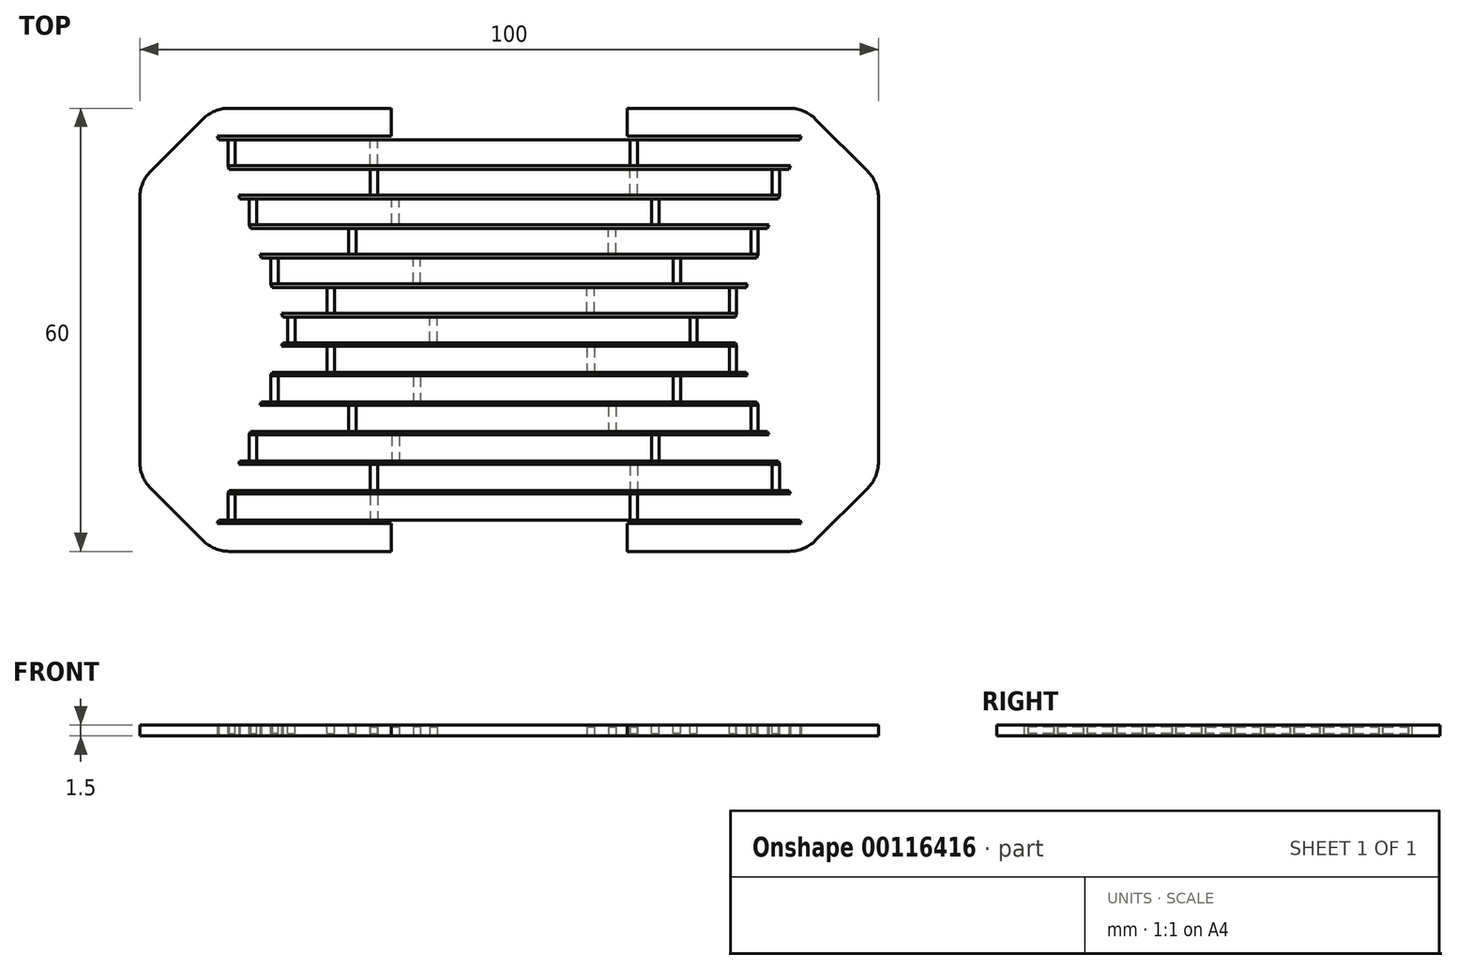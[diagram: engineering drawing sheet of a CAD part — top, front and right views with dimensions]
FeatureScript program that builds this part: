
annotation { "Feature Type Name" : "Feature", "Feature Type Description" : "" }
export const myFeature = defineFeature(function(context is Context, id is Id, definition is map)
    precondition{}
    {
        {
            var Q0;
            Q0=qCreatedBy(makeId("Top.planeOp"),FACE);
            var sketch = newSketch(context, id + "F0", { "sketchPlane" : qUnion([Q0])});
            skLineSegment(sketch, "E0.bottom", {"start": v(-50, 30) * mm, "end": v(-13.55, 30) * mm});
            skLineSegment(sketch, "E0.top", {"start": v(-50, -30) * mm, "end": v(-13.55, -30) * mm});
            skLineSegment(sketch, "E0.left", {"start": v(-50, 30) * mm, "end": v(-50, -30) * mm});
            skLineSegment(sketch, "E0.right", {"start": v(50, 30) * mm, "end": v(50, -30) * mm});
            skPoint(sketch, "E0.middle", {"position": v(0, 0) * mm});
            skLineSegment(sketch, "E1", {"start": v(-39.54, 26.25) * mm, "end": v(-39.36, 25.75) * mm});
            skLineSegment(sketch, "E2", {"start": v(-30.62, -1.75) * mm, "end": v(-30.8, -2.25) * mm});
            skLineSegment(sketch, "E3", {"start": v(-39.54, 26.25) * mm, "end": v(-13.55, 26.25) * mm});
            skLineSegment(sketch, "E4", {"start": v(-39.36, 25.75) * mm, "end": v(39.36, 25.75) * mm});
            skLineSegment(sketch, "E5", {"start": v(-38.08, 22.25) * mm, "end": v(38.08, 22.25) * mm});
            skLineSegment(sketch, "E6", {"start": v(-37.9, 21.75) * mm, "end": v(37.9, 21.75) * mm});
            skLineSegment(sketch, "E7.0.1.0", {"start": v(-36.63, 18.25) * mm, "end": v(36.63, 18.25) * mm});
            skLineSegment(sketch, "E7.0.1.1", {"start": v(-36.45, 17.75) * mm, "end": v(36.45, 17.75) * mm});
            skLineSegment(sketch, "E7.0.2.0", {"start": v(-35.17, 14.25) * mm, "end": v(35.17, 14.25) * mm});
            skLineSegment(sketch, "E7.0.2.1", {"start": v(-34.99, 13.75) * mm, "end": v(34.99, 13.75) * mm});
            skLineSegment(sketch, "E7.0.3.0", {"start": v(-33.72, 10.25) * mm, "end": v(33.72, 10.25) * mm});
            skLineSegment(sketch, "E7.0.3.1", {"start": v(-33.53, 9.75) * mm, "end": v(33.53, 9.75) * mm});
            skLineSegment(sketch, "E7.0.4.0", {"start": v(-27.23, 6.25) * mm, "end": v(32.26, 6.25) * mm});
            skLineSegment(sketch, "E7.0.4.1", {"start": v(-32.08, 5.75) * mm, "end": v(32.08, 5.75) * mm});
            skLineSegment(sketch, "E7.0.5.0", {"start": v(-30.8, 2.25) * mm, "end": v(30.8, 2.25) * mm});
            skLineSegment(sketch, "E7.0.5.1", {"start": v(-30.62, 1.75) * mm, "end": v(30.62, 1.75) * mm});
            skLineSegment(sketch, "E7.0.6.0", {"start": v(-30.62, -1.75) * mm, "end": v(30.62, -1.75) * mm});
            skLineSegment(sketch, "E7.0.6.1", {"start": v(-30.8, -2.25) * mm, "end": v(30.8, -2.25) * mm});
            skLineSegment(sketch, "E7.0.7.0", {"start": v(-32.08, -5.75) * mm, "end": v(32.08, -5.75) * mm});
            skLineSegment(sketch, "E7.0.7.1", {"start": v(-32.26, -6.25) * mm, "end": v(32.26, -6.25) * mm});
            skLineSegment(sketch, "E7.0.8.0", {"start": v(-33.53, -9.75) * mm, "end": v(33.53, -9.75) * mm});
            skLineSegment(sketch, "E7.0.8.1", {"start": v(-33.72, -10.25) * mm, "end": v(33.72, -10.25) * mm});
            skLineSegment(sketch, "E7.0.9.0", {"start": v(-34.99, -13.75) * mm, "end": v(34.99, -13.75) * mm});
            skLineSegment(sketch, "E7.0.9.1", {"start": v(-35.17, -14.25) * mm, "end": v(35.17, -14.25) * mm});
            skLineSegment(sketch, "E7.0.10.0", {"start": v(-36.45, -17.75) * mm, "end": v(36.45, -17.75) * mm});
            skLineSegment(sketch, "E7.0.10.1", {"start": v(-36.63, -18.25) * mm, "end": v(36.63, -18.25) * mm});
            skLineSegment(sketch, "E7.0.11.0", {"start": v(-37.9, -21.75) * mm, "end": v(37.9, -21.75) * mm});
            skLineSegment(sketch, "E7.0.11.1", {"start": v(-38.08, -22.25) * mm, "end": v(38.08, -22.25) * mm});
            skLineSegment(sketch, "E7.0.12.0", {"start": v(-39.36, -25.75) * mm, "end": v(39.36, -25.75) * mm});
            skLineSegment(sketch, "E7.0.12.1", {"start": v(-39.54, -26.25) * mm, "end": v(-13.55, -26.25) * mm});
            skLineSegment(sketch, "E7.direction1", {"start": v(-38.08, 22.25) * mm, "end": v(-35, 22.25) * mm, "construction": true});
            skLineSegment(sketch, "E7.direction2", {"start": v(-50, 22.25) * mm, "end": v(-50, 18.25) * mm, "construction": true});
            skLineSegment(sketch, "E8", {"start": v(-27.23, 30) * mm, "end": v(-27.23, -30) * mm, "construction": true});
            skPoint(sketch, "E9.orphan", {"position": v(-50, 21.75) * mm});
            skPoint(sketch, "E10.orphan", {"position": v(-50, 17.75) * mm});
            skPoint(sketch, "E11.orphan", {"position": v(-50, 14.25) * mm});
            skPoint(sketch, "E12.orphan", {"position": v(-50, 13.75) * mm});
            skPoint(sketch, "E13.orphan", {"position": v(-50, 10.25) * mm});
            skPoint(sketch, "E14.orphan", {"position": v(-50, 9.75) * mm});
            skPoint(sketch, "E15.orphan", {"position": v(-50, 6.25) * mm});
            skPoint(sketch, "E16.orphan", {"position": v(-50, 1.75) * mm});
            skPoint(sketch, "E17.orphan", {"position": v(-50, -5.75) * mm});
            skPoint(sketch, "E18.orphan", {"position": v(-50, -10.25) * mm});
            skPoint(sketch, "E19.orphan", {"position": v(-50, -14.25) * mm});
            skPoint(sketch, "E20.orphan", {"position": v(-50, -17.75) * mm});
            skPoint(sketch, "E21.orphan", {"position": v(-50, -22.25) * mm});
            skPoint(sketch, "E22.orphan", {"position": v(-50, -26.25) * mm});
            skPoint(sketch, "E23.orphan", {"position": v(-50, 5.75) * mm});
            skPoint(sketch, "E24.orphan", {"position": v(-50, 2.25) * mm});
            skPoint(sketch, "E25.orphan", {"position": v(-50, -2.25) * mm});
            skPoint(sketch, "E26.orphan", {"position": v(-50, -6.25) * mm});
            skPoint(sketch, "E27.orphan", {"position": v(-50, -9.75) * mm});
            skPoint(sketch, "E28.orphan", {"position": v(-50, -13.75) * mm});
            skPoint(sketch, "E29.orphan", {"position": v(-50, -18.25) * mm});
            skPoint(sketch, "E30.orphan", {"position": v(-50, -1.75) * mm});
            skPoint(sketch, "E31.orphan", {"position": v(-50, -21.75) * mm});
            skPoint(sketch, "E32.orphan", {"position": v(-50, -25.75) * mm});
            skLineSegment(sketch, "E33", {"start": v(-27.23, 6.25) * mm, "end": v(-32.26, 6.25) * mm});
            skPoint(sketch, "E34.orphan", {"position": v(50, 22.25) * mm});
            skPoint(sketch, "E35.orphan", {"position": v(50, 17.75) * mm});
            skPoint(sketch, "E36.orphan", {"position": v(50, 14.25) * mm});
            skPoint(sketch, "E37.orphan", {"position": v(50, 9.75) * mm});
            skPoint(sketch, "E38.orphan", {"position": v(50, 5.75) * mm});
            skPoint(sketch, "E39.orphan", {"position": v(50, 2.25) * mm});
            skPoint(sketch, "E40.orphan", {"position": v(50, -1.75) * mm});
            skPoint(sketch, "E41.orphan", {"position": v(50, -13.75) * mm});
            skPoint(sketch, "E42.orphan", {"position": v(50, -18.25) * mm});
            skPoint(sketch, "E43.orphan", {"position": v(50, -22.25) * mm});
            skPoint(sketch, "E44.orphan", {"position": v(50, -25.75) * mm});
            skPoint(sketch, "E45.orphan", {"position": v(50, -6.25) * mm});
            skPoint(sketch, "E46.orphan", {"position": v(50, -10.25) * mm});
            skPoint(sketch, "E47.orphan", {"position": v(50, 21.75) * mm});
            skPoint(sketch, "E48.orphan", {"position": v(50, 18.25) * mm});
            skPoint(sketch, "E49.orphan", {"position": v(50, 13.75) * mm});
            skPoint(sketch, "E50.orphan", {"position": v(50, 10.25) * mm});
            skPoint(sketch, "E51.orphan", {"position": v(50, 6.25) * mm});
            skPoint(sketch, "E52.orphan", {"position": v(50, 1.75) * mm});
            skPoint(sketch, "E53.orphan", {"position": v(50, -2.25) * mm});
            skPoint(sketch, "E54.orphan", {"position": v(50, -5.75) * mm});
            skPoint(sketch, "E55.orphan", {"position": v(50, -9.75) * mm});
            skPoint(sketch, "E56.orphan", {"position": v(50, -14.25) * mm});
            skPoint(sketch, "E57.orphan", {"position": v(50, -17.75) * mm});
            skPoint(sketch, "E58.orphan", {"position": v(50, -21.75) * mm});
            skPoint(sketch, "E59.orphan", {"position": v(50, -26.25) * mm});
            skPoint(sketch, "E60.orphan", {"position": v(-40.9, 30) * mm});
            skLineSegment(sketch, "E61.trimOffspring", {"start": v(-36.63, 18.25) * mm, "end": v(-36.45, 17.75) * mm});
            skLineSegment(sketch, "E62.trimOffspring", {"start": v(-33.72, 10.25) * mm, "end": v(-33.53, 9.75) * mm});
            skLineSegment(sketch, "E63.trimOffspring", {"start": v(-32.26, 6.25) * mm, "end": v(-32.08, 5.75) * mm});
            skLineSegment(sketch, "E64.trimOffspring", {"start": v(-30.8, 2.25) * mm, "end": v(-30.62, 1.75) * mm});
            skPoint(sketch, "E65.orphan", {"position": v(-29.99, 0) * mm});
            skLineSegment(sketch, "E66.trimOffspring", {"start": v(-32.08, -5.75) * mm, "end": v(-32.26, -6.25) * mm});
            skLineSegment(sketch, "E67.trimOffspring", {"start": v(-33.53, -9.75) * mm, "end": v(-33.72, -10.25) * mm});
            skLineSegment(sketch, "E68.trimOffspring", {"start": v(-34.99, -13.75) * mm, "end": v(-35.17, -14.25) * mm});
            skLineSegment(sketch, "E69.trimOffspring", {"start": v(-36.45, -17.75) * mm, "end": v(-36.63, -18.25) * mm});
            skLineSegment(sketch, "E70.trimOffspring", {"start": v(-39.36, -25.75) * mm, "end": v(-39.54, -26.25) * mm});
            skLineSegment(sketch, "E71.trimOffspring", {"start": v(-35.17, 14.25) * mm, "end": v(-34.99, 13.75) * mm});
            skPoint(sketch, "E72.orphan", {"position": v(-40.9, -30) * mm});
            skLineSegment(sketch, "E73.trimOffspring", {"start": v(13.55, 30) * mm, "end": v(50, 30) * mm});
            skLineSegment(sketch, "E74.trimOffspring", {"start": v(13.55, -30) * mm, "end": v(50, -30) * mm});
            skLineSegment(sketch, "E75", {"start": v(-13.55, 30) * mm, "end": v(-13.55, 26.25) * mm});
            skLineSegment(sketch, "E76", {"start": v(13.55, 30) * mm, "end": v(13.55, 26.25) * mm});
            skLineSegment(sketch, "E77", {"start": v(-13.55, -30) * mm, "end": v(-13.55, -26.25) * mm});
            skLineSegment(sketch, "E78", {"start": v(13.55, -30) * mm, "end": v(13.55, -26.25) * mm});
            skPoint(sketch, "E79.orphan", {"position": v(40.9, 30) * mm});
            skLineSegment(sketch, "E80.trimOffspring", {"start": v(38.08, 22.25) * mm, "end": v(37.9, 21.75) * mm});
            skLineSegment(sketch, "E81.trimOffspring", {"start": v(35.17, 14.25) * mm, "end": v(34.99, 13.75) * mm});
            skLineSegment(sketch, "E82.trimOffspring", {"start": v(32.26, 6.25) * mm, "end": v(32.08, 5.75) * mm});
            skPoint(sketch, "E83.orphan", {"position": v(29.99, 0) * mm});
            skLineSegment(sketch, "E84.trimOffspring", {"start": v(32.08, -5.75) * mm, "end": v(32.26, -6.25) * mm});
            skLineSegment(sketch, "E85.trimOffspring", {"start": v(36.45, -17.75) * mm, "end": v(36.63, -18.25) * mm});
            skPoint(sketch, "E86.orphan", {"position": v(40.9, -30) * mm});
            skLineSegment(sketch, "E87.trimOffspring", {"start": v(30.8, 2.25) * mm, "end": v(30.62, 1.75) * mm});
            skLineSegment(sketch, "E88.trimOffspring", {"start": v(33.53, -9.75) * mm, "end": v(33.72, -10.25) * mm});
            skLineSegment(sketch, "E89.trimOffspring", {"start": v(37.9, -21.75) * mm, "end": v(38.08, -22.25) * mm});
            skLineSegment(sketch, "E90.trimOffspring", {"start": v(39.36, -25.75) * mm, "end": v(39.54, -26.25) * mm});
            skLineSegment(sketch, "E91.trimOffspring", {"start": v(13.55, -26.25) * mm, "end": v(39.54, -26.25) * mm});
            skLineSegment(sketch, "E92.trimOffspring", {"start": v(13.55, 26.25) * mm, "end": v(39.54, 26.25) * mm});
            skLineSegment(sketch, "E93", {"start": v(39.54, 26.25) * mm, "end": v(39.36, 25.75) * mm});
            skLineSegment(sketch, "E94", {"start": v(36.63, 18.25) * mm, "end": v(36.45, 17.75) * mm});
            skLineSegment(sketch, "E95", {"start": v(33.72, 10.25) * mm, "end": v(33.53, 9.75) * mm});
            skLineSegment(sketch, "E96", {"start": v(30.62, -1.75) * mm, "end": v(30.8, -2.25) * mm});
            skLineSegment(sketch, "E97", {"start": v(34.99, -13.75) * mm, "end": v(35.17, -14.25) * mm});
            skLineSegment(sketch, "E98", {"start": v(-37.9, -21.75) * mm, "end": v(-38.08, -22.25) * mm});
            skLineSegment(sketch, "E99", {"start": v(-38.08, 22.25) * mm, "end": v(-37.9, 21.75) * mm});
            skSolve(sketch);
        }
        {
            var Q0;
            Q0 = qSketchRegion(id + "F0", true);
            extrude(context, id + "F1", {"entities" : qUnion([Q0]), "depth" : 1.5 * mm});
        }
        {
            var Q0;
            Q0=makeQuery(id+"F1.opExtrude","CAP_FACE",FACE,{"disambiguationData":[OSD([sQuery(id+"F0.wireOp",EDGE,"E0.bottom"),sQuery(id+"F0.wireOp",EDGE,"E0.top"),sQuery(id+"F0.wireOp",EDGE,"E0.left"),sQuery(id+"F0.wireOp",EDGE,"E0.right"),sQuery(id+"F0.wireOp",EDGE,"E1"),sQuery(id+"F0.wireOp",EDGE,"E2"),sQuery(id+"F0.wireOp",EDGE,"E3"),sQuery(id+"F0.wireOp",EDGE,"E4"),sQuery(id+"F0.wireOp",EDGE,"E5"),sQuery(id+"F0.wireOp",EDGE,"E6"),sQuery(id+"F0.wireOp",EDGE,"E7.0.1.0"),sQuery(id+"F0.wireOp",EDGE,"E7.0.1.1"),sQuery(id+"F0.wireOp",EDGE,"E7.0.2.0"),sQuery(id+"F0.wireOp",EDGE,"E7.0.2.1"),sQuery(id+"F0.wireOp",EDGE,"E7.0.3.0"),sQuery(id+"F0.wireOp",EDGE,"E7.0.3.1"),sQuery(id+"F0.wireOp",EDGE,"E7.0.4.0"),sQuery(id+"F0.wireOp",EDGE,"E7.0.4.1"),sQuery(id+"F0.wireOp",EDGE,"E7.0.5.0"),sQuery(id+"F0.wireOp",EDGE,"E7.0.5.1"),sQuery(id+"F0.wireOp",EDGE,"E7.0.6.0"),sQuery(id+"F0.wireOp",EDGE,"E7.0.6.1"),sQuery(id+"F0.wireOp",EDGE,"E7.0.7.0"),sQuery(id+"F0.wireOp",EDGE,"E7.0.7.1"),sQuery(id+"F0.wireOp",EDGE,"E7.0.8.0"),sQuery(id+"F0.wireOp",EDGE,"E7.0.8.1"),sQuery(id+"F0.wireOp",EDGE,"E7.0.9.0"),sQuery(id+"F0.wireOp",EDGE,"E7.0.9.1"),sQuery(id+"F0.wireOp",EDGE,"E7.0.10.0"),sQuery(id+"F0.wireOp",EDGE,"E7.0.10.1"),sQuery(id+"F0.wireOp",EDGE,"E7.0.11.0"),sQuery(id+"F0.wireOp",EDGE,"E7.0.11.1"),sQuery(id+"F0.wireOp",EDGE,"E7.0.12.0"),sQuery(id+"F0.wireOp",EDGE,"E7.0.12.1"),sQuery(id+"F0.wireOp",EDGE,"E33"),sQuery(id+"F0.wireOp",EDGE,"E61.trimOffspring"),sQuery(id+"F0.wireOp",EDGE,"E62.trimOffspring"),sQuery(id+"F0.wireOp",EDGE,"E63.trimOffspring"),sQuery(id+"F0.wireOp",EDGE,"E64.trimOffspring"),sQuery(id+"F0.wireOp",EDGE,"E66.trimOffspring"),sQuery(id+"F0.wireOp",EDGE,"E67.trimOffspring"),sQuery(id+"F0.wireOp",EDGE,"E68.trimOffspring"),sQuery(id+"F0.wireOp",EDGE,"E69.trimOffspring"),sQuery(id+"F0.wireOp",EDGE,"E70.trimOffspring"),sQuery(id+"F0.wireOp",EDGE,"E71.trimOffspring"),sQuery(id+"F0.wireOp",EDGE,"E73.trimOffspring"),sQuery(id+"F0.wireOp",EDGE,"E74.trimOffspring"),sQuery(id+"F0.wireOp",EDGE,"E75"),sQuery(id+"F0.wireOp",EDGE,"E76"),sQuery(id+"F0.wireOp",EDGE,"E77"),sQuery(id+"F0.wireOp",EDGE,"E78"),sQuery(id+"F0.wireOp",EDGE,"E80.trimOffspring"),sQuery(id+"F0.wireOp",EDGE,"E81.trimOffspring"),sQuery(id+"F0.wireOp",EDGE,"E82.trimOffspring"),sQuery(id+"F0.wireOp",EDGE,"E84.trimOffspring"),sQuery(id+"F0.wireOp",EDGE,"E85.trimOffspring"),sQuery(id+"F0.wireOp",EDGE,"E87.trimOffspring"),sQuery(id+"F0.wireOp",EDGE,"E88.trimOffspring"),sQuery(id+"F0.wireOp",EDGE,"E89.trimOffspring"),sQuery(id+"F0.wireOp",EDGE,"E90.trimOffspring"),sQuery(id+"F0.wireOp",EDGE,"E91.trimOffspring"),sQuery(id+"F0.wireOp",EDGE,"E92.trimOffspring"),sQuery(id+"F0.wireOp",EDGE,"E93"),sQuery(id+"F0.wireOp",EDGE,"E94"),sQuery(id+"F0.wireOp",EDGE,"E95"),sQuery(id+"F0.wireOp",EDGE,"E96"),sQuery(id+"F0.wireOp",EDGE,"E97"),sQuery(id+"F0.wireOp",EDGE,"E98"),sQuery(id+"F0.wireOp",EDGE,"E99")])],"isStart":false});
            var sketch = newSketch(context, id + "F2", { "sketchPlane" : qUnion([Q0])});
            skLineSegment(sketch, "E100.bottom", {"start": v(-38.08, 22.25) * mm, "end": v(-37.08, 22.25) * mm});
            skLineSegment(sketch, "E100.top", {"start": v(-38.08, 25.75) * mm, "end": v(-37.08, 25.75) * mm});
            skLineSegment(sketch, "E100.left", {"start": v(-38.08, 22.25) * mm, "end": v(-38.08, 25.75) * mm});
            skLineSegment(sketch, "E100.right", {"start": v(-37.08, 22.25) * mm, "end": v(-37.08, 25.75) * mm});
            skLineSegment(sketch, "E101.bottom", {"start": v(-35.17, 14.25) * mm, "end": v(-34.17, 14.25) * mm});
            skLineSegment(sketch, "E101.top", {"start": v(-35.17, 17.75) * mm, "end": v(-34.17, 17.75) * mm});
            skLineSegment(sketch, "E101.left", {"start": v(-35.17, 14.25) * mm, "end": v(-35.17, 17.75) * mm});
            skLineSegment(sketch, "E101.right", {"start": v(-34.17, 14.25) * mm, "end": v(-34.17, 17.75) * mm});
            skLineSegment(sketch, "E102.bottom", {"start": v(-32.26, 6.25) * mm, "end": v(-31.26, 6.25) * mm});
            skLineSegment(sketch, "E102.top", {"start": v(-32.26, 9.75) * mm, "end": v(-31.26, 9.75) * mm});
            skLineSegment(sketch, "E102.left", {"start": v(-32.26, 6.25) * mm, "end": v(-32.26, 9.75) * mm});
            skLineSegment(sketch, "E102.right", {"start": v(-31.26, 6.25) * mm, "end": v(-31.26, 9.75) * mm});
            skLineSegment(sketch, "E103.bottom", {"start": v(-29.99, 1.75) * mm, "end": v(-28.99, 1.75) * mm});
            skLineSegment(sketch, "E103.left", {"start": v(-29.99, 1.75) * mm, "end": v(-29.99, -1.75) * mm});
            skLineSegment(sketch, "E103.right", {"start": v(-28.99, 1.75) * mm, "end": v(-28.99, -1.75) * mm});
            skLineSegment(sketch, "E104.bottom", {"start": v(-17.82, 18.25) * mm, "end": v(-18.82, 18.25) * mm});
            skLineSegment(sketch, "E104.top", {"start": v(-17.82, 21.75) * mm, "end": v(-18.82, 21.75) * mm});
            skLineSegment(sketch, "E104.left", {"start": v(-17.82, 18.25) * mm, "end": v(-17.82, 21.75) * mm});
            skLineSegment(sketch, "E104.right", {"start": v(-18.82, 18.25) * mm, "end": v(-18.82, 21.75) * mm});
            skLineSegment(sketch, "E105.bottom", {"start": v(-20.74, 10.25) * mm, "end": v(-21.74, 10.25) * mm});
            skLineSegment(sketch, "E105.top", {"start": v(-20.74, 13.75) * mm, "end": v(-21.74, 13.75) * mm});
            skLineSegment(sketch, "E105.left", {"start": v(-20.74, 10.25) * mm, "end": v(-20.74, 13.75) * mm});
            skLineSegment(sketch, "E105.right", {"start": v(-21.74, 10.25) * mm, "end": v(-21.74, 13.75) * mm});
            skLineSegment(sketch, "E106.bottom", {"start": v(-23.65, 2.25) * mm, "end": v(-24.65, 2.25) * mm});
            skLineSegment(sketch, "E106.top", {"start": v(-23.65, 5.75) * mm, "end": v(-24.65, 5.75) * mm});
            skLineSegment(sketch, "E106.left", {"start": v(-23.65, 2.25) * mm, "end": v(-23.65, 5.75) * mm});
            skLineSegment(sketch, "E106.right", {"start": v(-24.65, 2.25) * mm, "end": v(-24.65, 5.75) * mm});
            skLineSegment(sketch, "E107.bottom", {"start": v(-15.97, 26.25) * mm, "end": v(-9.47, 26.25) * mm});
            skLineSegment(sketch, "E107.top", {"start": v(-15.97, 31.35) * mm, "end": v(-9.47, 31.35) * mm});
            skLineSegment(sketch, "E107.left", {"start": v(-15.97, 26.25) * mm, "end": v(-15.97, 31.35) * mm});
            skLineSegment(sketch, "E107.right", {"start": v(-9.47, 26.25) * mm, "end": v(-9.47, 31.35) * mm});
            skLineSegment(sketch, "E108.MirrorCS", {"start": v(36.63, 21.75) * mm, "end": v(35.63, 21.75) * mm});
            skLineSegment(sketch, "E109.MirrorCS", {"start": v(36.63, 18.25) * mm, "end": v(35.63, 18.25) * mm});
            skLineSegment(sketch, "E110.MirrorCS", {"start": v(33.72, 13.75) * mm, "end": v(32.72, 13.75) * mm});
            skLineSegment(sketch, "E111.MirrorCS", {"start": v(16.37, 25.75) * mm, "end": v(17.37, 25.75) * mm});
            skLineSegment(sketch, "E112.MirrorCS", {"start": v(19.28, 14.25) * mm, "end": v(20.28, 14.25) * mm});
            skLineSegment(sketch, "E113.MirrorCS", {"start": v(33.72, 10.25) * mm, "end": v(32.72, 10.25) * mm});
            skLineSegment(sketch, "E114.MirrorCS", {"start": v(35.63, 18.25) * mm, "end": v(35.63, 21.75) * mm});
            skLineSegment(sketch, "E115.MirrorCS", {"start": v(36.63, 18.25) * mm, "end": v(36.63, 21.75) * mm});
            skLineSegment(sketch, "E116.MirrorCS", {"start": v(32.72, 10.25) * mm, "end": v(32.72, 13.75) * mm});
            skLineSegment(sketch, "E117.MirrorCS", {"start": v(33.72, 10.25) * mm, "end": v(33.72, 13.75) * mm});
            skLineSegment(sketch, "E118.MirrorCS", {"start": v(24.47, 1.75) * mm, "end": v(24.47, -1.75) * mm});
            skLineSegment(sketch, "E119.MirrorCS", {"start": v(30.8, 2.25) * mm, "end": v(30.8, 5.75) * mm});
            skLineSegment(sketch, "E120.MirrorCS", {"start": v(19.28, 14.25) * mm, "end": v(19.28, 17.75) * mm});
            skLineSegment(sketch, "E121.MirrorCS", {"start": v(29.8, 2.25) * mm, "end": v(29.8, 5.75) * mm});
            skLineSegment(sketch, "E122.MirrorCS", {"start": v(20.28, 14.25) * mm, "end": v(20.28, 17.75) * mm});
            skLineSegment(sketch, "E123.MirrorCS", {"start": v(25.47, 1.75) * mm, "end": v(25.47, -1.75) * mm});
            skLineSegment(sketch, "E124.MirrorCS", {"start": v(19.28, 17.75) * mm, "end": v(20.28, 17.75) * mm});
            skLineSegment(sketch, "E125.MirrorCS", {"start": v(30.8, 2.25) * mm, "end": v(29.8, 2.25) * mm});
            skLineSegment(sketch, "E126.MirrorCS", {"start": v(23.2, 6.25) * mm, "end": v(23.2, 9.75) * mm});
            skLineSegment(sketch, "E127.MirrorCS", {"start": v(30.8, 5.75) * mm, "end": v(29.8, 5.75) * mm});
            skLineSegment(sketch, "E128.MirrorCS", {"start": v(16.37, 22.25) * mm, "end": v(17.37, 22.25) * mm});
            skLineSegment(sketch, "E129.MirrorCS", {"start": v(22.2, 9.75) * mm, "end": v(23.2, 9.75) * mm});
            skLineSegment(sketch, "E130.MirrorCS", {"start": v(22.2, 6.25) * mm, "end": v(22.2, 9.75) * mm});
            skLineSegment(sketch, "E131.MirrorCS", {"start": v(17.37, 22.25) * mm, "end": v(17.37, 25.75) * mm});
            skLineSegment(sketch, "E132.MirrorCS", {"start": v(16.37, 22.25) * mm, "end": v(16.37, 25.75) * mm});
            skLineSegment(sketch, "E133.MirrorCS", {"start": v(24.47, 1.75) * mm, "end": v(25.47, 1.75) * mm});
            skLineSegment(sketch, "E134.MirrorCS", {"start": v(22.2, 6.25) * mm, "end": v(23.2, 6.25) * mm});
            skLineSegment(sketch, "E135.MirrorCS", {"start": v(15.97, 26.25) * mm, "end": v(15.97, 31.35) * mm});
            skLineSegment(sketch, "E136.MirrorCS", {"start": v(15.97, 26.25) * mm, "end": v(9.47, 26.25) * mm});
            skLineSegment(sketch, "E137.MirrorCS", {"start": v(9.47, 26.25) * mm, "end": v(9.47, 31.35) * mm});
            skLineSegment(sketch, "E138", {"start": v(24.47, -1.75) * mm, "end": v(25.47, -1.75) * mm});
            skLineSegment(sketch, "E139", {"start": v(-29.99, -1.75) * mm, "end": v(-28.99, -1.75) * mm});
            skLineSegment(sketch, "E140", {"start": v(9.47, 31.35) * mm, "end": v(15.97, 31.35) * mm});
            skLineSegment(sketch, "E141.MirrorCS", {"start": v(-17.82, -18.25) * mm, "end": v(-18.82, -18.25) * mm});
            skLineSegment(sketch, "E142.MirrorCS", {"start": v(16.37, -22.25) * mm, "end": v(17.37, -22.25) * mm});
            skLineSegment(sketch, "E143.MirrorCS", {"start": v(-20.74, -10.25) * mm, "end": v(-21.74, -10.25) * mm});
            skLineSegment(sketch, "E144.MirrorCS", {"start": v(33.72, -10.25) * mm, "end": v(32.72, -10.25) * mm});
            skLineSegment(sketch, "E145.MirrorCS", {"start": v(22.2, -9.75) * mm, "end": v(23.2, -9.75) * mm});
            skLineSegment(sketch, "E146.MirrorCS", {"start": v(36.63, -21.75) * mm, "end": v(35.63, -21.75) * mm});
            skLineSegment(sketch, "E147.MirrorCS", {"start": v(-23.65, -5.75) * mm, "end": v(-24.65, -5.75) * mm});
            skLineSegment(sketch, "E148.MirrorCS", {"start": v(22.2, -6.25) * mm, "end": v(23.2, -6.25) * mm});
            skLineSegment(sketch, "E149.MirrorCS", {"start": v(-32.26, -9.75) * mm, "end": v(-31.26, -9.75) * mm});
            skLineSegment(sketch, "E150.MirrorCS", {"start": v(19.28, -14.25) * mm, "end": v(20.28, -14.25) * mm});
            skLineSegment(sketch, "E151.MirrorCS", {"start": v(16.37, -25.75) * mm, "end": v(17.37, -25.75) * mm});
            skLineSegment(sketch, "E152.MirrorCS", {"start": v(-17.82, -21.75) * mm, "end": v(-18.82, -21.75) * mm});
            skLineSegment(sketch, "E153.MirrorCS", {"start": v(-20.74, -13.75) * mm, "end": v(-21.74, -13.75) * mm});
            skLineSegment(sketch, "E154.MirrorCS", {"start": v(30.8, -5.75) * mm, "end": v(29.8, -5.75) * mm});
            skLineSegment(sketch, "E155.MirrorCS", {"start": v(-32.26, -6.25) * mm, "end": v(-31.26, -6.25) * mm});
            skLineSegment(sketch, "E156.MirrorCS", {"start": v(36.63, -18.25) * mm, "end": v(35.63, -18.25) * mm});
            skLineSegment(sketch, "E157.MirrorCS", {"start": v(-35.17, -14.25) * mm, "end": v(-34.17, -14.25) * mm});
            skLineSegment(sketch, "E158.MirrorCS", {"start": v(-35.17, -17.75) * mm, "end": v(-34.17, -17.75) * mm});
            skLineSegment(sketch, "E159.MirrorCS", {"start": v(33.72, -13.75) * mm, "end": v(32.72, -13.75) * mm});
            skLineSegment(sketch, "E160.MirrorCS", {"start": v(19.28, -17.75) * mm, "end": v(20.28, -17.75) * mm});
            skLineSegment(sketch, "E161.MirrorCS", {"start": v(-38.08, -22.25) * mm, "end": v(-37.08, -22.25) * mm});
            skLineSegment(sketch, "E162.MirrorCS", {"start": v(-38.08, -25.75) * mm, "end": v(-37.08, -25.75) * mm});
            skLineSegment(sketch, "E163.MirrorCS", {"start": v(-9.47, -26.25) * mm, "end": v(-9.47, -31.35) * mm});
            skLineSegment(sketch, "E164.MirrorCS", {"start": v(19.28, -14.25) * mm, "end": v(19.28, -17.75) * mm});
            skLineSegment(sketch, "E165.MirrorCS", {"start": v(-34.17, -14.25) * mm, "end": v(-34.17, -17.75) * mm});
            skLineSegment(sketch, "E166.MirrorCS", {"start": v(-23.65, -2.25) * mm, "end": v(-23.65, -5.75) * mm});
            skLineSegment(sketch, "E167.MirrorCS", {"start": v(30.8, -2.25) * mm, "end": v(30.8, -5.75) * mm});
            skLineSegment(sketch, "E168.MirrorCS", {"start": v(-15.97, -26.25) * mm, "end": v(-15.97, -31.35) * mm});
            skLineSegment(sketch, "E169.MirrorCS", {"start": v(-18.82, -18.25) * mm, "end": v(-18.82, -21.75) * mm});
            skLineSegment(sketch, "E170.MirrorCS", {"start": v(15.97, -26.25) * mm, "end": v(9.47, -26.25) * mm});
            skLineSegment(sketch, "E171.MirrorCS", {"start": v(17.37, -22.25) * mm, "end": v(17.37, -25.75) * mm});
            skLineSegment(sketch, "E172.MirrorCS", {"start": v(-24.65, -2.25) * mm, "end": v(-24.65, -5.75) * mm});
            skLineSegment(sketch, "E173.MirrorCS", {"start": v(-15.97, -31.35) * mm, "end": v(-9.47, -31.35) * mm});
            skLineSegment(sketch, "E174.MirrorCS", {"start": v(9.47, -26.25) * mm, "end": v(9.47, -31.35) * mm});
            skLineSegment(sketch, "E175.MirrorCS", {"start": v(-31.26, -6.25) * mm, "end": v(-31.26, -9.75) * mm});
            skLineSegment(sketch, "E176.MirrorCS", {"start": v(-32.26, -6.25) * mm, "end": v(-32.26, -9.75) * mm});
            skLineSegment(sketch, "E177.MirrorCS", {"start": v(-20.74, -10.25) * mm, "end": v(-20.74, -13.75) * mm});
            skLineSegment(sketch, "E178.MirrorCS", {"start": v(-38.08, -22.25) * mm, "end": v(-38.08, -25.75) * mm});
            skLineSegment(sketch, "E179.MirrorCS", {"start": v(20.28, -14.25) * mm, "end": v(20.28, -17.75) * mm});
            skLineSegment(sketch, "E180.MirrorCS", {"start": v(-15.97, -26.25) * mm, "end": v(-9.47, -26.25) * mm});
            skLineSegment(sketch, "E181.MirrorCS", {"start": v(15.97, -26.25) * mm, "end": v(15.97, -31.35) * mm});
            skLineSegment(sketch, "E182.MirrorCS", {"start": v(-21.74, -10.25) * mm, "end": v(-21.74, -13.75) * mm});
            skLineSegment(sketch, "E183.MirrorCS", {"start": v(9.47, -31.35) * mm, "end": v(15.97, -31.35) * mm});
            skLineSegment(sketch, "E184.MirrorCS", {"start": v(-17.82, -18.25) * mm, "end": v(-17.82, -21.75) * mm});
            skLineSegment(sketch, "E185.MirrorCS", {"start": v(-35.17, -14.25) * mm, "end": v(-35.17, -17.75) * mm});
            skLineSegment(sketch, "E186.MirrorCS", {"start": v(-23.65, -2.25) * mm, "end": v(-24.65, -2.25) * mm});
            skLineSegment(sketch, "E187.MirrorCS", {"start": v(29.8, -2.25) * mm, "end": v(29.8, -5.75) * mm});
            skLineSegment(sketch, "E188.MirrorCS", {"start": v(30.8, -2.25) * mm, "end": v(29.8, -2.25) * mm});
            skLineSegment(sketch, "E189.MirrorCS", {"start": v(23.2, -6.25) * mm, "end": v(23.2, -9.75) * mm});
            skLineSegment(sketch, "E190.MirrorCS", {"start": v(35.63, -18.25) * mm, "end": v(35.63, -21.75) * mm});
            skLineSegment(sketch, "E191.MirrorCS", {"start": v(-37.08, -22.25) * mm, "end": v(-37.08, -25.75) * mm});
            skLineSegment(sketch, "E192.MirrorCS", {"start": v(16.37, -22.25) * mm, "end": v(16.37, -25.75) * mm});
            skLineSegment(sketch, "E193.MirrorCS", {"start": v(32.72, -10.25) * mm, "end": v(32.72, -13.75) * mm});
            skLineSegment(sketch, "E194.MirrorCS", {"start": v(22.2, -6.25) * mm, "end": v(22.2, -9.75) * mm});
            skLineSegment(sketch, "E195.MirrorCS", {"start": v(36.63, -18.25) * mm, "end": v(36.63, -21.75) * mm});
            skLineSegment(sketch, "E196.MirrorCS", {"start": v(33.72, -10.25) * mm, "end": v(33.72, -13.75) * mm});
            skSolve(sketch);
        }
        {
            var Q0;
            Q0 = qSketchRegion(id + "F2", true);
            extrude(context, id + "F3", {"entities" : qUnion([Q0]), "operationType" : NewBodyOperationType.REMOVE, "oppositeDirection" : true, "depth" : 1.2 * mm});
        }
        {
            var Q0;
            Q0=makeQuery(id+"F1.opExtrude","CAP_FACE",FACE,{"disambiguationData":[OSD([sQuery(id+"F0.wireOp",EDGE,"E0.bottom"),sQuery(id+"F0.wireOp",EDGE,"E0.top"),sQuery(id+"F0.wireOp",EDGE,"E0.left"),sQuery(id+"F0.wireOp",EDGE,"E0.right"),sQuery(id+"F0.wireOp",EDGE,"E1"),sQuery(id+"F0.wireOp",EDGE,"E2"),sQuery(id+"F0.wireOp",EDGE,"E3"),sQuery(id+"F0.wireOp",EDGE,"E4"),sQuery(id+"F0.wireOp",EDGE,"E5"),sQuery(id+"F0.wireOp",EDGE,"E6"),sQuery(id+"F0.wireOp",EDGE,"E7.0.1.0"),sQuery(id+"F0.wireOp",EDGE,"E7.0.1.1"),sQuery(id+"F0.wireOp",EDGE,"E7.0.2.0"),sQuery(id+"F0.wireOp",EDGE,"E7.0.2.1"),sQuery(id+"F0.wireOp",EDGE,"E7.0.3.0"),sQuery(id+"F0.wireOp",EDGE,"E7.0.3.1"),sQuery(id+"F0.wireOp",EDGE,"E7.0.4.0"),sQuery(id+"F0.wireOp",EDGE,"E7.0.4.1"),sQuery(id+"F0.wireOp",EDGE,"E7.0.5.0"),sQuery(id+"F0.wireOp",EDGE,"E7.0.5.1"),sQuery(id+"F0.wireOp",EDGE,"E7.0.6.0"),sQuery(id+"F0.wireOp",EDGE,"E7.0.6.1"),sQuery(id+"F0.wireOp",EDGE,"E7.0.7.0"),sQuery(id+"F0.wireOp",EDGE,"E7.0.7.1"),sQuery(id+"F0.wireOp",EDGE,"E7.0.8.0"),sQuery(id+"F0.wireOp",EDGE,"E7.0.8.1"),sQuery(id+"F0.wireOp",EDGE,"E7.0.9.0"),sQuery(id+"F0.wireOp",EDGE,"E7.0.9.1"),sQuery(id+"F0.wireOp",EDGE,"E7.0.10.0"),sQuery(id+"F0.wireOp",EDGE,"E7.0.10.1"),sQuery(id+"F0.wireOp",EDGE,"E7.0.11.0"),sQuery(id+"F0.wireOp",EDGE,"E7.0.11.1"),sQuery(id+"F0.wireOp",EDGE,"E7.0.12.0"),sQuery(id+"F0.wireOp",EDGE,"E7.0.12.1"),sQuery(id+"F0.wireOp",EDGE,"E33"),sQuery(id+"F0.wireOp",EDGE,"E61.trimOffspring"),sQuery(id+"F0.wireOp",EDGE,"E62.trimOffspring"),sQuery(id+"F0.wireOp",EDGE,"E63.trimOffspring"),sQuery(id+"F0.wireOp",EDGE,"E64.trimOffspring"),sQuery(id+"F0.wireOp",EDGE,"E66.trimOffspring"),sQuery(id+"F0.wireOp",EDGE,"E67.trimOffspring"),sQuery(id+"F0.wireOp",EDGE,"E68.trimOffspring"),sQuery(id+"F0.wireOp",EDGE,"E69.trimOffspring"),sQuery(id+"F0.wireOp",EDGE,"E70.trimOffspring"),sQuery(id+"F0.wireOp",EDGE,"E71.trimOffspring"),sQuery(id+"F0.wireOp",EDGE,"E73.trimOffspring"),sQuery(id+"F0.wireOp",EDGE,"E74.trimOffspring"),sQuery(id+"F0.wireOp",EDGE,"E75"),sQuery(id+"F0.wireOp",EDGE,"E76"),sQuery(id+"F0.wireOp",EDGE,"E77"),sQuery(id+"F0.wireOp",EDGE,"E78"),sQuery(id+"F0.wireOp",EDGE,"E80.trimOffspring"),sQuery(id+"F0.wireOp",EDGE,"E81.trimOffspring"),sQuery(id+"F0.wireOp",EDGE,"E82.trimOffspring"),sQuery(id+"F0.wireOp",EDGE,"E84.trimOffspring"),sQuery(id+"F0.wireOp",EDGE,"E85.trimOffspring"),sQuery(id+"F0.wireOp",EDGE,"E87.trimOffspring"),sQuery(id+"F0.wireOp",EDGE,"E88.trimOffspring"),sQuery(id+"F0.wireOp",EDGE,"E89.trimOffspring"),sQuery(id+"F0.wireOp",EDGE,"E90.trimOffspring"),sQuery(id+"F0.wireOp",EDGE,"E91.trimOffspring"),sQuery(id+"F0.wireOp",EDGE,"E92.trimOffspring"),sQuery(id+"F0.wireOp",EDGE,"E93"),sQuery(id+"F0.wireOp",EDGE,"E94"),sQuery(id+"F0.wireOp",EDGE,"E95"),sQuery(id+"F0.wireOp",EDGE,"E96"),sQuery(id+"F0.wireOp",EDGE,"E97"),sQuery(id+"F0.wireOp",EDGE,"E98"),sQuery(id+"F0.wireOp",EDGE,"E99")])],"isStart":true});
            var sketch = newSketch(context, id + "F4", { "sketchPlane" : qUnion([Q0])});
            skLineSegment(sketch, "E197", {"start": v(-21.64, -30) * mm, "end": v(-10.73, 0) * mm, "construction": true});
            skLineSegment(sketch, "E198", {"start": v(-10.73, 0) * mm, "end": v(-21.64, 30) * mm, "construction": true});
            skLineSegment(sketch, "E199.bottom", {"start": v(-18.82, -22.25) * mm, "end": v(-17.82, -22.25) * mm});
            skLineSegment(sketch, "E199.top", {"start": v(-18.82, -25.75) * mm, "end": v(-17.82, -25.75) * mm});
            skLineSegment(sketch, "E199.left", {"start": v(-18.82, -22.25) * mm, "end": v(-18.82, -25.75) * mm});
            skLineSegment(sketch, "E199.right", {"start": v(-17.82, -22.25) * mm, "end": v(-17.82, -25.75) * mm});
            skLineSegment(sketch, "E200.bottom", {"start": v(-15.91, -14.25) * mm, "end": v(-14.91, -14.25) * mm});
            skLineSegment(sketch, "E200.top", {"start": v(-15.91, -17.75) * mm, "end": v(-14.91, -17.75) * mm});
            skLineSegment(sketch, "E200.left", {"start": v(-15.91, -14.25) * mm, "end": v(-15.91, -17.75) * mm});
            skLineSegment(sketch, "E200.right", {"start": v(-14.91, -14.25) * mm, "end": v(-14.91, -17.75) * mm});
            skLineSegment(sketch, "E201.bottom", {"start": v(-13, -6.25) * mm, "end": v(-12, -6.25) * mm});
            skLineSegment(sketch, "E201.top", {"start": v(-13, -9.75) * mm, "end": v(-12, -9.75) * mm});
            skLineSegment(sketch, "E201.left", {"start": v(-13, -6.25) * mm, "end": v(-13, -9.75) * mm});
            skLineSegment(sketch, "E201.right", {"start": v(-12, -6.25) * mm, "end": v(-12, -9.75) * mm});
            skLineSegment(sketch, "E202.MirrorCS", {"start": v(21.64, -30) * mm, "end": v(10.73, 0) * mm, "construction": true});
            skLineSegment(sketch, "E203.bottom", {"start": v(17.37, -18.25) * mm, "end": v(16.37, -18.25) * mm});
            skLineSegment(sketch, "E203.top", {"start": v(17.37, -21.75) * mm, "end": v(16.37, -21.75) * mm});
            skLineSegment(sketch, "E203.left", {"start": v(17.37, -18.25) * mm, "end": v(17.37, -21.75) * mm});
            skLineSegment(sketch, "E203.right", {"start": v(16.37, -18.25) * mm, "end": v(16.37, -21.75) * mm});
            skLineSegment(sketch, "E204.bottom", {"start": v(14.46, -10.25) * mm, "end": v(13.46, -10.25) * mm});
            skLineSegment(sketch, "E204.top", {"start": v(14.46, -13.75) * mm, "end": v(13.46, -13.75) * mm});
            skLineSegment(sketch, "E204.left", {"start": v(14.46, -10.25) * mm, "end": v(14.46, -13.75) * mm});
            skLineSegment(sketch, "E204.right", {"start": v(13.46, -10.25) * mm, "end": v(13.46, -13.75) * mm});
            skLineSegment(sketch, "E205.bottom", {"start": v(11.54, -2.25) * mm, "end": v(10.54, -2.25) * mm});
            skLineSegment(sketch, "E205.top", {"start": v(11.54, -5.75) * mm, "end": v(10.54, -5.75) * mm});
            skLineSegment(sketch, "E205.left", {"start": v(11.54, -2.25) * mm, "end": v(11.54, -5.75) * mm});
            skLineSegment(sketch, "E205.right", {"start": v(10.54, -2.25) * mm, "end": v(10.54, -5.75) * mm});
            skLineSegment(sketch, "E206.MirrorCS", {"start": v(14.46, 13.75) * mm, "end": v(13.46, 13.75) * mm});
            skLineSegment(sketch, "E207.MirrorCS", {"start": v(14.46, 10.25) * mm, "end": v(13.46, 10.25) * mm});
            skLineSegment(sketch, "E208.MirrorCS", {"start": v(-15.91, 14.25) * mm, "end": v(-14.91, 14.25) * mm});
            skLineSegment(sketch, "E209.MirrorCS", {"start": v(-15.91, 17.75) * mm, "end": v(-14.91, 17.75) * mm});
            skLineSegment(sketch, "E210.MirrorCS", {"start": v(17.37, 18.25) * mm, "end": v(16.37, 18.25) * mm});
            skLineSegment(sketch, "E211.MirrorCS", {"start": v(-18.82, 25.75) * mm, "end": v(-17.82, 25.75) * mm});
            skLineSegment(sketch, "E212.MirrorCS", {"start": v(-18.82, 22.25) * mm, "end": v(-17.82, 22.25) * mm});
            skLineSegment(sketch, "E213.MirrorCS", {"start": v(-13, 6.25) * mm, "end": v(-12, 6.25) * mm});
            skLineSegment(sketch, "E214.MirrorCS", {"start": v(-13, 9.75) * mm, "end": v(-12, 9.75) * mm});
            skLineSegment(sketch, "E215.MirrorCS", {"start": v(11.54, 5.75) * mm, "end": v(10.54, 5.75) * mm});
            skLineSegment(sketch, "E216.MirrorCS", {"start": v(11.54, 2.25) * mm, "end": v(10.54, 2.25) * mm});
            skLineSegment(sketch, "E217.MirrorCS", {"start": v(17.37, 21.75) * mm, "end": v(16.37, 21.75) * mm});
            skLineSegment(sketch, "E218.MirrorCS", {"start": v(-17.82, 22.25) * mm, "end": v(-17.82, 25.75) * mm});
            skLineSegment(sketch, "E219.MirrorCS", {"start": v(10.54, 2.25) * mm, "end": v(10.54, 5.75) * mm});
            skLineSegment(sketch, "E220.MirrorCS", {"start": v(-12, 6.25) * mm, "end": v(-12, 9.75) * mm});
            skLineSegment(sketch, "E221.MirrorCS", {"start": v(16.37, 18.25) * mm, "end": v(16.37, 21.75) * mm});
            skLineSegment(sketch, "E222.MirrorCS", {"start": v(11.54, 2.25) * mm, "end": v(11.54, 5.75) * mm});
            skLineSegment(sketch, "E223.MirrorCS", {"start": v(-18.82, 22.25) * mm, "end": v(-18.82, 25.75) * mm});
            skLineSegment(sketch, "E224.MirrorCS", {"start": v(-15.91, 14.25) * mm, "end": v(-15.91, 17.75) * mm});
            skLineSegment(sketch, "E225.MirrorCS", {"start": v(-14.91, 14.25) * mm, "end": v(-14.91, 17.75) * mm});
            skLineSegment(sketch, "E226.MirrorCS", {"start": v(-13, 6.25) * mm, "end": v(-13, 9.75) * mm});
            skLineSegment(sketch, "E227.MirrorCS", {"start": v(17.37, 18.25) * mm, "end": v(17.37, 21.75) * mm});
            skLineSegment(sketch, "E228.MirrorCS", {"start": v(14.46, 10.25) * mm, "end": v(14.46, 13.75) * mm});
            skLineSegment(sketch, "E229.MirrorCS", {"start": v(13.46, 10.25) * mm, "end": v(13.46, 13.75) * mm});
            skLineSegment(sketch, "E230.bottom", {"start": v(-10.73, 1.75) * mm, "end": v(-9.73, 1.75) * mm});
            skLineSegment(sketch, "E230.top", {"start": v(-10.73, -1.75) * mm, "end": v(-9.73, -1.75) * mm});
            skLineSegment(sketch, "E230.left", {"start": v(-10.73, 1.75) * mm, "end": v(-10.73, -1.75) * mm});
            skLineSegment(sketch, "E230.right", {"start": v(-9.73, 1.75) * mm, "end": v(-9.73, -1.75) * mm});
            skSolve(sketch);
        }
        {
            var Q0;
            Q0 = qSketchRegion(id + "F4", true);
            extrude(context, id + "F5", {"entities" : qUnion([Q0]), "operationType" : NewBodyOperationType.REMOVE, "oppositeDirection" : true, "depth" : 1.2 * mm});
        }
        {
            var Q0;
            {var subQ0=sQuery(id+"F0.wireOp",EDGE,"E98");var subQ1=sQuery(id+"F0.wireOp",EDGE,"E0.top");var subQ2=sQuery(id+"F0.wireOp",EDGE,"E71.trimOffspring");var subQ3=sQuery(id+"F0.wireOp",EDGE,"E70.trimOffspring");var subQ4=sQuery(id+"F0.wireOp",EDGE,"E69.trimOffspring");var subQ5=sQuery(id+"F0.wireOp",EDGE,"E67.trimOffspring");var subQ6=sQuery(id+"F0.wireOp",EDGE,"E68.trimOffspring");var subQ7=sQuery(id+"F0.wireOp",EDGE,"E66.trimOffspring");var subQ8=sQuery(id+"F0.wireOp",EDGE,"E64.trimOffspring");var subQ9=sQuery(id+"F0.wireOp",EDGE,"E62.trimOffspring");var subQ10=sQuery(id+"F0.wireOp",EDGE,"E63.trimOffspring");var subQ11=sQuery(id+"F0.wireOp",EDGE,"E61.trimOffspring");var subQ12=sQuery(id+"F0.wireOp",EDGE,"E7.0.12.0");var subQ13=sQuery(id+"F0.wireOp",EDGE,"E7.0.11.0");var subQ14=sQuery(id+"F0.wireOp",EDGE,"E7.0.8.1");var subQ15=sQuery(id+"F0.wireOp",EDGE,"E7.0.10.0");var subQ16=sQuery(id+"F0.wireOp",EDGE,"E7.0.1.1");var subQ17=sQuery(id+"F0.wireOp",EDGE,"E99");var subQ18=sQuery(id+"F0.wireOp",EDGE,"E7.0.5.0");var subQ19=sQuery(id+"F0.wireOp",EDGE,"E7.0.1.0");var subQ20=sQuery(id+"F0.wireOp",EDGE,"E6");var subQ21=sQuery(id+"F0.wireOp",EDGE,"E4");var subQ22=sQuery(id+"F0.wireOp",EDGE,"E7.0.3.0");var subQ23=sQuery(id+"F0.wireOp",EDGE,"E3");var subQ24=sQuery(id+"F0.wireOp",EDGE,"E2");var subQ25=sQuery(id+"F0.wireOp",EDGE,"E7.0.12.1");var subQ26=sQuery(id+"F0.wireOp",EDGE,"E0.bottom");var subQ27=sQuery(id+"F0.wireOp",EDGE,"E7.0.8.0");var subQ28=sQuery(id+"F0.wireOp",EDGE,"E0.left");var subQ29=sQuery(id+"F0.wireOp",EDGE,"E1");var subQ30=sQuery(id+"F0.wireOp",EDGE,"E7.0.7.0");var subQ31=sQuery(id+"F0.wireOp",EDGE,"E7.0.2.1");var subQ32=sQuery(id+"F0.wireOp",EDGE,"E7.0.6.0");var subQ33=sQuery(id+"F0.wireOp",EDGE,"E7.0.4.1");var subQ34=sQuery(id+"F0.wireOp",EDGE,"E7.0.3.1");var subQ35=sQuery(id+"F0.wireOp",EDGE,"E7.0.9.0");var subQ36=sQuery(id+"F0.wireOp",EDGE,"E7.0.10.1");var subQ37=sQuery(id+"F0.wireOp",EDGE,"E7.0.6.1");var subQ38=sQuery(id+"F0.wireOp",EDGE,"E7.0.5.1");Q0=makeQuery(id+"F3.boolean.opBoolean","SPLIT",FACE,{"disambiguationData":[TD([makeQuery(id+"F1.opExtrude","SWEPT_FACE",FACE,{"disambiguationData":[OSD([subQ26])]})])],"derivedFrom":makeQuery(id+"F1.opExtrude","CAP_FACE",FACE,{"disambiguationData":[OSD([subQ26,subQ1,subQ28,sQuery(id+"F0.wireOp",EDGE,"E0.right"),subQ29,subQ24,subQ23,subQ21,sQuery(id+"F0.wireOp",EDGE,"E5"),subQ20,subQ19,subQ16,sQuery(id+"F0.wireOp",EDGE,"E7.0.2.0"),subQ31,subQ22,subQ34,sQuery(id+"F0.wireOp",EDGE,"E7.0.4.0"),subQ33,subQ18,subQ38,subQ32,subQ37,subQ30,sQuery(id+"F0.wireOp",EDGE,"E7.0.7.1"),subQ27,subQ14,subQ35,sQuery(id+"F0.wireOp",EDGE,"E7.0.9.1"),subQ15,subQ36,subQ13,sQuery(id+"F0.wireOp",EDGE,"E7.0.11.1"),subQ12,subQ25,sQuery(id+"F0.wireOp",EDGE,"E33"),subQ11,subQ9,subQ10,subQ8,subQ7,subQ5,subQ6,subQ4,subQ3,subQ2,sQuery(id+"F0.wireOp",EDGE,"E73.trimOffspring"),sQuery(id+"F0.wireOp",EDGE,"E74.trimOffspring"),sQuery(id+"F0.wireOp",EDGE,"E75"),sQuery(id+"F0.wireOp",EDGE,"E76"),sQuery(id+"F0.wireOp",EDGE,"E77"),sQuery(id+"F0.wireOp",EDGE,"E78"),sQuery(id+"F0.wireOp",EDGE,"E80.trimOffspring"),sQuery(id+"F0.wireOp",EDGE,"E81.trimOffspring"),sQuery(id+"F0.wireOp",EDGE,"E82.trimOffspring"),sQuery(id+"F0.wireOp",EDGE,"E84.trimOffspring"),sQuery(id+"F0.wireOp",EDGE,"E85.trimOffspring"),sQuery(id+"F0.wireOp",EDGE,"E87.trimOffspring"),sQuery(id+"F0.wireOp",EDGE,"E88.trimOffspring"),sQuery(id+"F0.wireOp",EDGE,"E89.trimOffspring"),sQuery(id+"F0.wireOp",EDGE,"E90.trimOffspring"),sQuery(id+"F0.wireOp",EDGE,"E91.trimOffspring"),sQuery(id+"F0.wireOp",EDGE,"E92.trimOffspring"),sQuery(id+"F0.wireOp",EDGE,"E93"),sQuery(id+"F0.wireOp",EDGE,"E94"),sQuery(id+"F0.wireOp",EDGE,"E95"),sQuery(id+"F0.wireOp",EDGE,"E96"),sQuery(id+"F0.wireOp",EDGE,"E97"),subQ0,subQ17])],"isStart":false})});}
            var sketch = newSketch(context, id + "F6", { "sketchPlane" : qUnion([Q0])});
            skLineSegment(sketch, "E231.bottom", {"start": v(-15.97, 30) * mm, "end": v(15.97, 30) * mm});
            skLineSegment(sketch, "E231.top", {"start": v(-15.97, 26.06) * mm, "end": v(15.97, 26.06) * mm});
            skLineSegment(sketch, "E231.left", {"start": v(-15.97, 30) * mm, "end": v(-15.97, 26.06) * mm});
            skLineSegment(sketch, "E231.right", {"start": v(15.97, 30) * mm, "end": v(15.97, 26.06) * mm});
            skLineSegment(sketch, "E232.bottom", {"start": v(-15.97, -26.25) * mm, "end": v(15.97, -26.25) * mm});
            skLineSegment(sketch, "E232.top", {"start": v(-15.97, -33.25) * mm, "end": v(15.97, -33.25) * mm});
            skLineSegment(sketch, "E232.left", {"start": v(-15.97, -26.25) * mm, "end": v(-15.97, -33.25) * mm});
            skLineSegment(sketch, "E233", {"start": v(15.97, -33.25) * mm, "end": v(15.97, -26.25) * mm});
            skSolve(sketch);
        }
        {
            var Q0;
            Q0 = qSketchRegion(id + "F6", true);
            extrude(context, id + "F7", {"entities" : qUnion([Q0]), "operationType" : NewBodyOperationType.REMOVE, "oppositeDirection" : true, "depth" : 25 * mm});
        }
        {
            var Q0;
            Q0=makeQuery(id+"F1.opExtrude","SWEPT_EDGE",EDGE,{"disambiguationData":[OSD([sQuery(id+"F0.wireOp",EDGE,"E0.top"),sQuery(id+"F0.wireOp",EDGE,"E0.left")])]});
            var Q1;
            Q1=makeQuery(id+"F1.opExtrude","SWEPT_EDGE",EDGE,{"disambiguationData":[OSD([sQuery(id+"F0.wireOp",EDGE,"E0.right"),sQuery(id+"F0.wireOp",EDGE,"E74.trimOffspring")])]});
            var Q2;
            Q2=makeQuery(id+"F1.opExtrude","SWEPT_EDGE",EDGE,{"disambiguationData":[OSD([sQuery(id+"F0.wireOp",EDGE,"E0.right"),sQuery(id+"F0.wireOp",EDGE,"E73.trimOffspring")])]});
            var Q3;
            Q3=makeQuery(id+"F1.opExtrude","SWEPT_EDGE",EDGE,{"disambiguationData":[OSD([sQuery(id+"F0.wireOp",EDGE,"E0.bottom"),sQuery(id+"F0.wireOp",EDGE,"E0.left")])]});
            chamfer(context, id + "F8", {"entities" : qUnion([Q0, Q1, Q2, Q3]), "width" : 10 * mm, "tangentPropagation" : true});
        }
        {
            var Q0;
            {var subQ0=sQuery(id+"F0.wireOp",EDGE,"E0.left");Q0=makeQuery(id+"F8.opChamfer","BLEND_EDGE",EDGE,{"blendedFrom":[makeQuery(id+"F1.opExtrude","SWEPT_EDGE",EDGE,{"disambiguationData":[OSD([sQuery(id+"F0.wireOp",EDGE,"E0.bottom"),subQ0])]}),makeQuery(id+"F1.opExtrude","SWEPT_FACE",FACE,{"disambiguationData":[OSD([subQ0])]})],"blendedInto":[makeQuery(id+"F1.opExtrude","SWEPT_FACE",FACE,{"disambiguationData":[OSD([subQ0])]})]});}
            var Q1;
            {var subQ0=sQuery(id+"F0.wireOp",EDGE,"E0.bottom");Q1=makeQuery(id+"F8.opChamfer","BLEND_EDGE",EDGE,{"blendedFrom":[makeQuery(id+"F1.opExtrude","SWEPT_EDGE",EDGE,{"disambiguationData":[OSD([subQ0,sQuery(id+"F0.wireOp",EDGE,"E0.left")])]}),makeQuery(id+"F1.opExtrude","SWEPT_FACE",FACE,{"disambiguationData":[OSD([subQ0])]})],"blendedInto":[makeQuery(id+"F1.opExtrude","SWEPT_FACE",FACE,{"disambiguationData":[OSD([subQ0])]})]});}
            var Q2;
            {var subQ0=sQuery(id+"F0.wireOp",EDGE,"E0.left");Q2=makeQuery(id+"F8.opChamfer","BLEND_EDGE",EDGE,{"blendedFrom":[makeQuery(id+"F1.opExtrude","SWEPT_EDGE",EDGE,{"disambiguationData":[OSD([sQuery(id+"F0.wireOp",EDGE,"E0.top"),subQ0])]}),makeQuery(id+"F1.opExtrude","SWEPT_FACE",FACE,{"disambiguationData":[OSD([subQ0])]})],"blendedInto":[makeQuery(id+"F1.opExtrude","SWEPT_FACE",FACE,{"disambiguationData":[OSD([subQ0])]})]});}
            var Q3;
            {var subQ0=sQuery(id+"F0.wireOp",EDGE,"E0.top");Q3=makeQuery(id+"F8.opChamfer","BLEND_EDGE",EDGE,{"blendedFrom":[makeQuery(id+"F1.opExtrude","SWEPT_EDGE",EDGE,{"disambiguationData":[OSD([subQ0,sQuery(id+"F0.wireOp",EDGE,"E0.left")])]}),makeQuery(id+"F1.opExtrude","SWEPT_FACE",FACE,{"disambiguationData":[OSD([subQ0])]})],"blendedInto":[makeQuery(id+"F1.opExtrude","SWEPT_FACE",FACE,{"disambiguationData":[OSD([subQ0])]})]});}
            var Q4;
            {var subQ0=sQuery(id+"F0.wireOp",EDGE,"E74.trimOffspring");Q4=makeQuery(id+"F8.opChamfer","BLEND_EDGE",EDGE,{"blendedFrom":[makeQuery(id+"F1.opExtrude","SWEPT_EDGE",EDGE,{"disambiguationData":[OSD([sQuery(id+"F0.wireOp",EDGE,"E0.right"),subQ0])]}),makeQuery(id+"F1.opExtrude","SWEPT_FACE",FACE,{"disambiguationData":[OSD([subQ0])]})],"blendedInto":[makeQuery(id+"F1.opExtrude","SWEPT_FACE",FACE,{"disambiguationData":[OSD([subQ0])]})]});}
            var Q5;
            {var subQ0=sQuery(id+"F0.wireOp",EDGE,"E0.right");Q5=makeQuery(id+"F8.opChamfer","BLEND_EDGE",EDGE,{"blendedFrom":[makeQuery(id+"F1.opExtrude","SWEPT_EDGE",EDGE,{"disambiguationData":[OSD([subQ0,sQuery(id+"F0.wireOp",EDGE,"E74.trimOffspring")])]}),makeQuery(id+"F1.opExtrude","SWEPT_FACE",FACE,{"disambiguationData":[OSD([subQ0])]})],"blendedInto":[makeQuery(id+"F1.opExtrude","SWEPT_FACE",FACE,{"disambiguationData":[OSD([subQ0])]})]});}
            var Q6;
            {var subQ0=sQuery(id+"F0.wireOp",EDGE,"E0.right");Q6=makeQuery(id+"F8.opChamfer","BLEND_EDGE",EDGE,{"blendedFrom":[makeQuery(id+"F1.opExtrude","SWEPT_EDGE",EDGE,{"disambiguationData":[OSD([subQ0,sQuery(id+"F0.wireOp",EDGE,"E73.trimOffspring")])]}),makeQuery(id+"F1.opExtrude","SWEPT_FACE",FACE,{"disambiguationData":[OSD([subQ0])]})],"blendedInto":[makeQuery(id+"F1.opExtrude","SWEPT_FACE",FACE,{"disambiguationData":[OSD([subQ0])]})]});}
            var Q7;
            {var subQ0=sQuery(id+"F0.wireOp",EDGE,"E73.trimOffspring");Q7=makeQuery(id+"F8.opChamfer","BLEND_EDGE",EDGE,{"blendedFrom":[makeQuery(id+"F1.opExtrude","SWEPT_EDGE",EDGE,{"disambiguationData":[OSD([sQuery(id+"F0.wireOp",EDGE,"E0.right"),subQ0])]}),makeQuery(id+"F1.opExtrude","SWEPT_FACE",FACE,{"disambiguationData":[OSD([subQ0])]})],"blendedInto":[makeQuery(id+"F1.opExtrude","SWEPT_FACE",FACE,{"disambiguationData":[OSD([subQ0])]})]});}
            fillet(context, id + "F9", {"entities" : qUnion([Q0, Q1, Q2, Q3, Q4, Q5, Q6, Q7]), "radius" : 5 * mm, "tangentPropagation" : true, "allowEdgeOverflow" : false});
        }
    });
